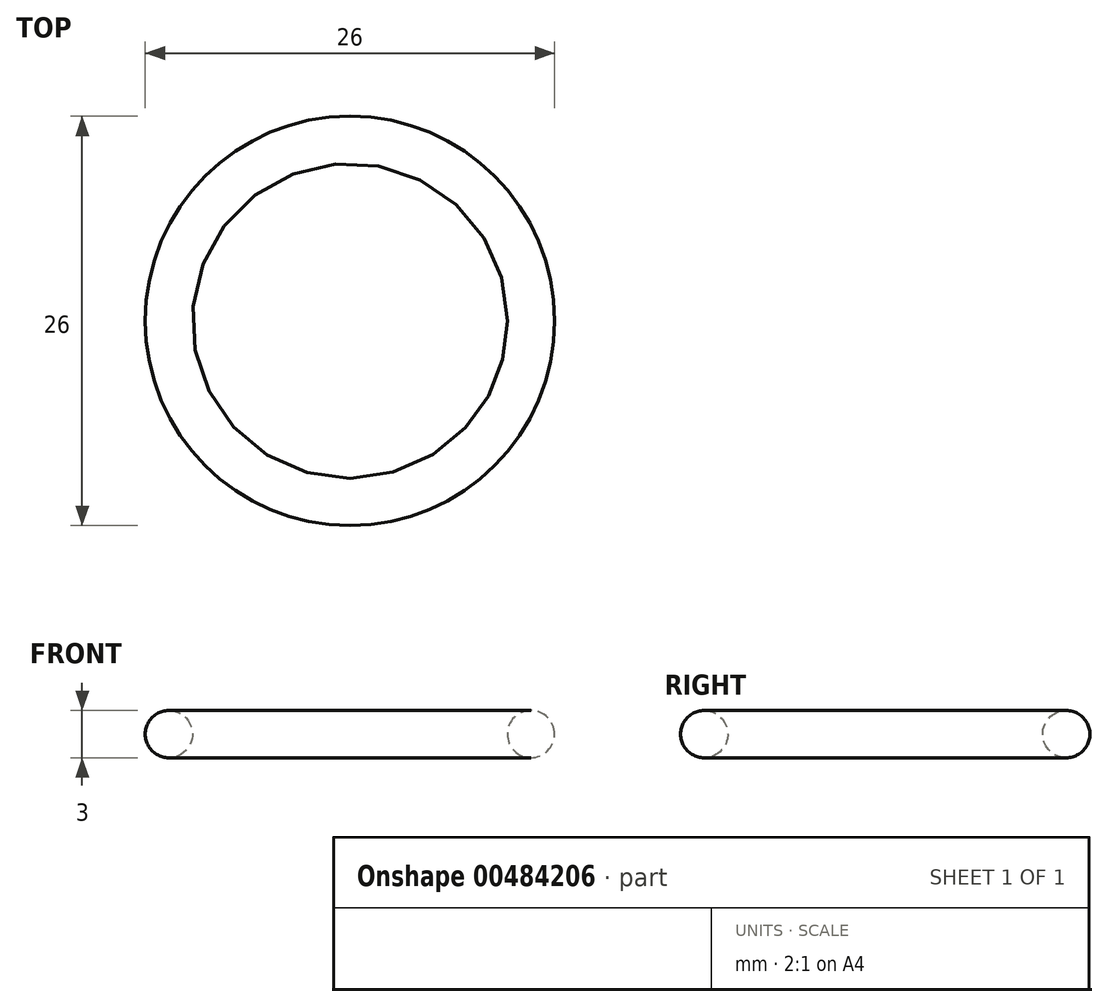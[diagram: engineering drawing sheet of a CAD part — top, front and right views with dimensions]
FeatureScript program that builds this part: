
annotation { "Feature Type Name" : "Feature", "Feature Type Description" : "" }
export const myFeature = defineFeature(function(context is Context, id is Id, definition is map)
    precondition{}
    {
        {
            var Q0;
            Q0=qCreatedBy(makeId("Front.planeOp"),FACE);
            var sketch = newSketch(context, id + "F0", { "sketchPlane" : qUnion([Q0])});
            skCircle(sketch, "E0", {"center": v(0, 0) * mm, "radius": 1.5 * mm});
            skLineSegment(sketch, "E1", {"start": v(-11.5, 5.56) * mm, "end": v(-11.5, -6.46) * mm});
            skSolve(sketch);
        }
        {
            var Q0;
            Q0=makeQuery(id+"F0.imprint","IMPRINT",FACE,{"disambiguationData":[TD([[makeQuery(id+"F0.imprint","IMPRINT",EDGE,{"derivedFrom":sQuery(id+"F0.wireOp",EDGE,"E0")}),1.0]])]});
            var Q1;
            Q1=sQuery(id+"F0.wireOp",EDGE,"E1");
            revolve(context, id + "F1", {"entities" : qUnion([Q0]), "axis" : qUnion([Q1]), "revolveType" : RevolveType.FULL});
        }
    });
